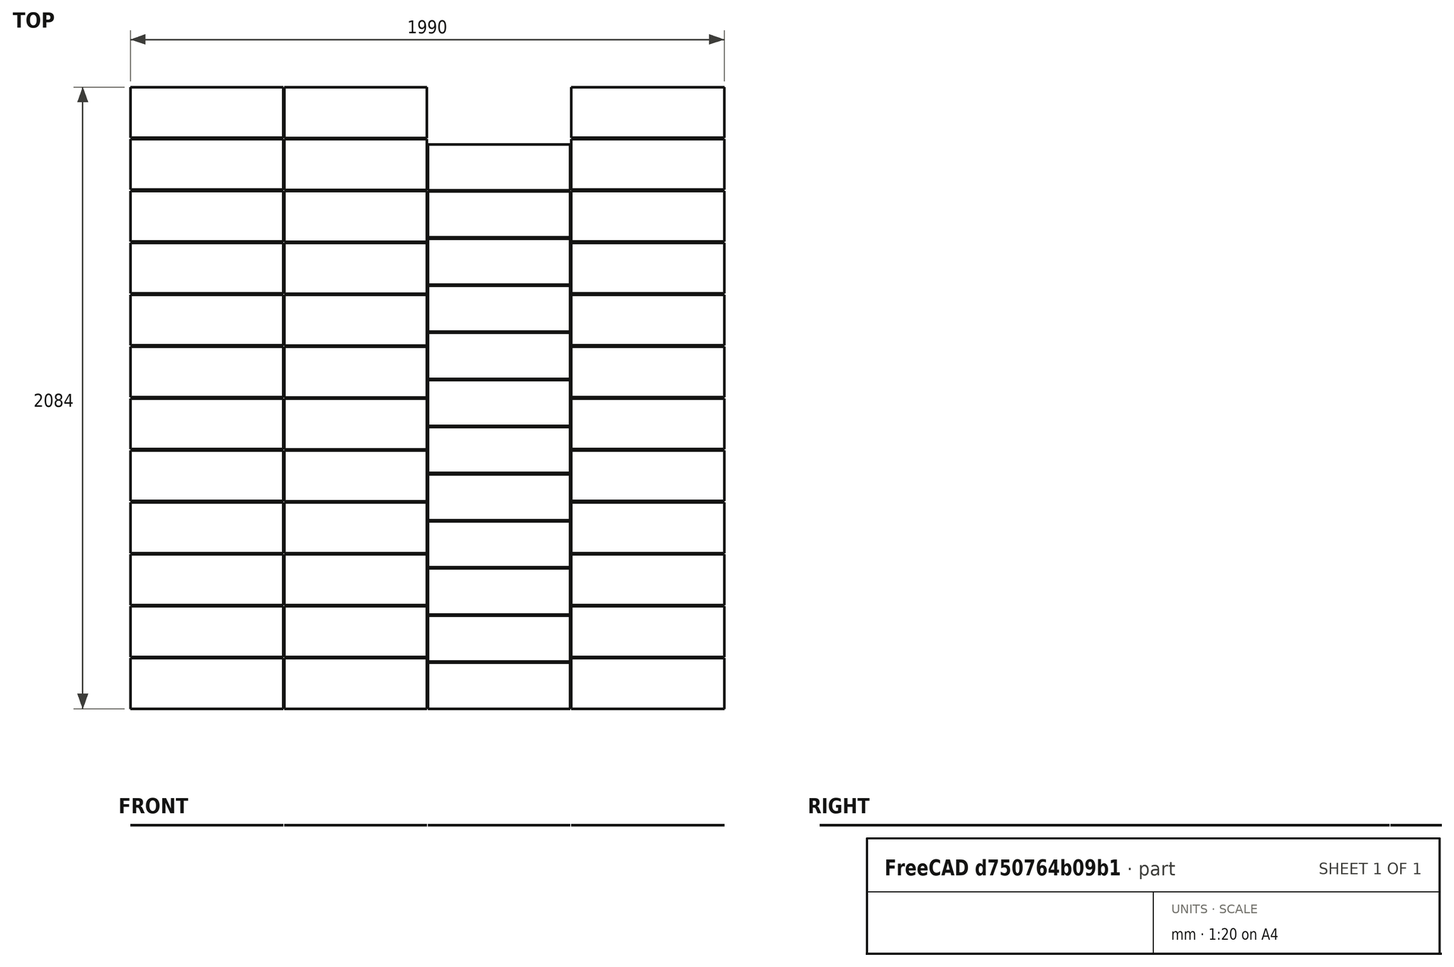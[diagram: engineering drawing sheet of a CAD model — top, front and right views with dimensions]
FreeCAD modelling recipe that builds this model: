
FCSTD DOCUMENT  (FreeCAD 1.0RUnknown)
Label: Schnittplan
License: All rights reserved
LicenseURL: https://en.wikipedia.org/wiki/All_rights_reserved
objects: Part::Part2DObjectPython×34, App::FeaturePython×28, Part::FeaturePython×4
note: 38 computed .brp shape members not serialized (recipe doc carries the construction recipe); baked Part::Feature solids carry a one-line shape summary decoded from their .brp

FEATURE [Part::Part2DObjectPython] Rectangle  label="3-Schichtplatte Fichte 19mm"  # Draft 2D object (typed FeaturePython)
  Area = 10250000
  ChamferSize = 0
  Columns = 1
  FilletRadius = 0
  Height = 5000
  Length = 2050
  MakeFace = true
  Rows = 1
FEATURE [Part::Part2DObjectPython] Rectangle001  label="Seitenteil Korpus 1"  # Draft 2D object (typed FeaturePython)
  Area = 1204200
  ChamferSize = 0
  Columns = 1
  FilletRadius = 0
  Height = 2007
  Length = 600
  MakeFace = true
  Placement = pos=(0,600,0) rot=(0,0,1;-1.5708rad)
  Rows = 1
FEATURE [Part::Part2DObjectPython] Rectangle002  label="Seitenteil Korpus 1.1"  # Draft 2D object (typed FeaturePython)
  Area = 1204200
  ChamferSize = 0
  Columns = 1
  FilletRadius = 0
  Height = 2007
  Length = 600
  MakeFace = true
  Placement = pos=(0,1204,0) rot=(0,0,1;-1.5708rad)
  Rows = 1
FEATURE [Part::Part2DObjectPython] Rectangle003  label="Tür Korpus 2"  # Draft 2D object (typed FeaturePython)
  Area = 1094610
  ChamferSize = 0
  Columns = 1
  FilletRadius = 0
  Height = 2046
  Length = 535
  MakeFace = true
  Placement = pos=(0,1743,0) rot=(0,0,1;-1.5708rad)
  Rows = 1
FEATURE [Part::Part2DObjectPython] Rectangle004  label="Tür Korpus 1"  # Draft 2D object (typed FeaturePython)
  Area = 1305400
  ChamferSize = 0
  Columns = 1
  FilletRadius = 0
  Height = 2440
  Length = 535
  MakeFace = true
  Placement = pos=(0,1747,0) rot=(0,0,1;0rad)
  Rows = 1
FEATURE [Part::Part2DObjectPython] Rectangle005  label="Rückplatte Korpus 1"  # Draft 2D object (typed FeaturePython)
  Area = 1104300
  ChamferSize = 0
  Columns = 1
  FilletRadius = 0
  Height = 2045
  Length = 540
  MakeFace = true
  Placement = pos=(2100,540,0) rot=(0,0,1;-1.5708rad)
  Rows = 1
FEATURE [Part::Part2DObjectPython] Rectangle006  label="Rückplatte Korpus 2"  # Draft 2D object (typed FeaturePython)
  Area = 764100
  ChamferSize = 0
  Columns = 1
  FilletRadius = 0
  Height = 1415
  Length = 540
  MakeFace = true
  Placement = pos=(539,4034,0) rot=(0,0,1;-1.5708rad)
  Rows = 1
FEATURE [Part::Part2DObjectPython] Rectangle007  label="Rückplatte Korpus 3"  # Draft 2D object (typed FeaturePython)
  Area = 421200
  ChamferSize = 0
  Columns = 1
  FilletRadius = 0
  Height = 780
  Length = 540
  MakeFace = true
  Placement = pos=(3188,3776,0) rot=(0,0,1;-1.5708rad)
  Rows = 1
FEATURE [Part::Part2DObjectPython] Rectangle008  label="Tür Korpus 3"  # Draft 2D object (typed FeaturePython)
  Area = 756490
  ChamferSize = 0
  Columns = 1
  FilletRadius = 0
  Height = 1414
  Length = 535
  MakeFace = true
  Placement = pos=(539,2282,0) rot=(0,0,1;-1.5708rad)
  Rows = 1
FEATURE [Part::Part2DObjectPython] Rectangle009  label="Tür Korpus 4"  # Draft 2D object (typed FeaturePython)
  Area = 402730
  ChamferSize = 0
  Columns = 1
  FilletRadius = 0
  Height = 782
  Length = 515
  MakeFace = true
  Placement = pos=(0,4191,0) rot=(0,0,1;0rad)
  Rows = 1
FEATURE [Part::Part2DObjectPython] Rectangle010  label="Rückplatte Korpus 4"  # Draft 2D object (typed FeaturePython)
  Area = 408200
  ChamferSize = 0
  Columns = 1
  FilletRadius = 0
  Height = 785
  Length = 520
  MakeFace = true
  Placement = pos=(2704,4964,0) rot=(0,0,1;-1.5708rad)
  Rows = 1
FEATURE [Part::Part2DObjectPython] Rectangle011  label="Seitenteil Korpus 2"  # Draft 2D object (typed FeaturePython)
  Area = 826200
  ChamferSize = 0
  Columns = 1
  FilletRadius = 0
  Height = 1377
  Length = 600
  MakeFace = true
  Placement = pos=(539,2886,0) rot=(0,0,1;-1.5708rad)
  Rows = 1
FEATURE [Part::Part2DObjectPython] Rectangle012  label="Seitenteil Korpus 2.1"  # Draft 2D object (typed FeaturePython)
  Area = 826200
  ChamferSize = 0
  Columns = 1
  FilletRadius = 0
  Height = 1377
  Length = 600
  MakeFace = true
  Placement = pos=(539,3490,0) rot=(0,0,1;-1.5708rad)
  Rows = 1
FEATURE [Part::Part2DObjectPython] Rectangle013  label="3-Schichtplatte Fichte 19mm001"  # Draft 2D object (typed FeaturePython)
  Area = 10250000
  ChamferSize = 0
  Columns = 1
  FilletRadius = 0
  Height = 5000
  Length = 2050
  MakeFace = true
  Placement = pos=(2100,0,0) rot=(0,0,1;0rad)
  Rows = 1
FEATURE [Part::Part2DObjectPython] Rectangle014  label="Seitenteil Korpus 3"  # Draft 2D object (typed FeaturePython)
  Area = 445200
  ChamferSize = 0
  Columns = 1
  FilletRadius = 0
  Height = 742
  Length = 600
  MakeFace = true
  Placement = pos=(2100,3232,0) rot=(0,0,1;-1.5708rad)
  Rows = 1
FEATURE [Part::Part2DObjectPython] Rectangle015  label="Seitenteil Korpus 3.1"  # Draft 2D object (typed FeaturePython)
  Area = 445200
  ChamferSize = 0
  Columns = 1
  FilletRadius = 0
  Height = 742
  Length = 600
  MakeFace = true
  Placement = pos=(2846,3232,0) rot=(0,0,1;-1.5708rad)
  Rows = 1
FEATURE [Part::Part2DObjectPython] Rectangle016  label="Schublade Seitenteile"  # Draft 2D object (typed FeaturePython)
  Area = 87040
  ChamferSize = 0
  Columns = 1
  FilletRadius = 0
  Height = 170
  Length = 512
  MakeFace = true
  Placement = pos=(3592,544,0) rot=(0,0,1;0rad)
  Rows = 1
FEATURE [Part::Part2DObjectPython] Line  # Draft 2D object (typed FeaturePython)
  Area = 0
  ChamferSize = 0
  Closed = false
  End = (2100,2458,0)
  FilletRadius = 0
  Length = 1914
  MakeFace = true
  Placement = pos=(2345.23,716.413,0) rot=(0,0,1;0rad)
  Points = (2) [(-245.23,-172.413,0),(-245.23,1741.59,0)]
  Start = (2100,544,0)
  Subdivisions = 0
FEATURE [Part::FeaturePython] PathArray  # WARN: FeaturePython — macro-defined, semantics opaque (R4)
  Align = false
  AlignMode = 0
  Base = -> Rectangle016
  Count = 12
  EndOffset = 0
  ExtraTranslation = (0,0,0)
  ForceVertical = false
  Fuse = false
  PathObject = -> Line
  StartOffset = 0
  TangentVector = (1,0,0)
  VerticalVector = (0,0,1)
FEATURE [Part::Part2DObjectPython] Rectangle017  label="Schublade Fronten"  # Draft 2D object (typed FeaturePython)
  Area = 81090
  ChamferSize = 0
  Columns = 1
  FilletRadius = 0
  Height = 170
  Length = 477
  MakeFace = true
  Placement = pos=(3111,1148,0) rot=(0,0,1;0rad)
  Rows = 1
FEATURE [Part::Part2DObjectPython] Line001  # Draft 2D object (typed FeaturePython)
  Area = 0
  ChamferSize = 0
  Closed = false
  End = (2616,2457.4,0)
  FilletRadius = 0
  Length = 1913.4
  MakeFace = true
  Placement = pos=(2616,564,0) rot=(0,0,1;0rad)
  Points = (2) [(0,-20,0),(0,1893.4,0)]
  Start = (2616,544,0)
  Subdivisions = 0
FEATURE [Part::FeaturePython] PathArray001  # WARN: FeaturePython — macro-defined, semantics opaque (R4)
  Align = false
  AlignMode = 0
  Base = -> Rectangle017
  Count = 12
  EndOffset = 0
  ExtraTranslation = (0,0,0)
  ForceVertical = false
  Fuse = false
  PathObject = -> Line001
  StartOffset = 0
  TangentVector = (1,0,0)
  VerticalVector = (0,0,1)
FEATURE [Part::Part2DObjectPython] Rectangle018  label="Schublade Rückplatten"  # Draft 2D object (typed FeaturePython)
  Area = 73458
  ChamferSize = 0
  Columns = 1
  FilletRadius = 0
  Height = 154
  Length = 477
  MakeFace = true
  Placement = pos=(2630,1148,0) rot=(0,0,1;0rad)
  Rows = 1
FEATURE [Part::Part2DObjectPython] Line002  # Draft 2D object (typed FeaturePython)
  Area = 0
  ChamferSize = 0
  Closed = false
  End = (3097,2282,0)
  FilletRadius = 0
  Length = 1738
  MakeFace = true
  Placement = pos=(3100,589,0) rot=(0,0,1;0rad)
  Points = (2) [(-3,-45,0),(-3,1693,0)]
  Start = (3097,544,0)
  Subdivisions = 0
FEATURE [Part::FeaturePython] PathArray002  # WARN: FeaturePython — macro-defined, semantics opaque (R4)
  Align = false
  AlignMode = 0
  Base = -> Rectangle018
  Count = 12
  EndOffset = 0
  ExtraTranslation = (0,0,0)
  ForceVertical = false
  Fuse = false
  PathObject = -> Line002
  StartOffset = 0
  TangentVector = (1,0,0)
  VerticalVector = (0,0,1)
FEATURE [Part::Part2DObjectPython] Line003  # Draft 2D object (typed FeaturePython)
  Area = 0
  ChamferSize = 0
  Closed = false
  End = (3578,2458,0)
  FilletRadius = 0
  Length = 1914
  MakeFace = true
  Placement = pos=(3826,716,0) rot=(0,0,1;0rad)
  Points = (2) [(-248,-172,0),(-248,1742,0)]
  Start = (3578,544,0)
  Subdivisions = 0
FEATURE [Part::Part2DObjectPython] Rectangle019  label="Schublade Seitenteile001"  # Draft 2D object (typed FeaturePython)
  Area = 87040
  ChamferSize = 0
  Columns = 1
  FilletRadius = 0
  Height = 170
  Length = 512
  MakeFace = true
  Placement = pos=(3592,544,0) rot=(0,0,1;0rad)
  Rows = 1
FEATURE [Part::FeaturePython] PathArray003  # WARN: FeaturePython — macro-defined, semantics opaque (R4)
  Align = false
  AlignMode = 0
  Base = -> Rectangle019
  Count = 12
  EndOffset = 0
  ExtraTranslation = (0,0,0)
  ForceVertical = false
  Fuse = false
  PathObject = -> Line003
  StartOffset = 0
  TangentVector = (1,0,0)
  VerticalVector = (0,0,1)
FEATURE [Part::Part2DObjectPython] Rectangle020  label="Deckplatten Korpus 1-3"  # Draft 2D object (typed FeaturePython)
  Area = 324000
  ChamferSize = 0
  Columns = 1
  FilletRadius = 0
  Height = 540
  Length = 600
  MakeFace = true
  Placement = pos=(3592,3232,0) rot=(0,0,1;-1.5708rad)
  Rows = 1
FEATURE [Part::Part2DObjectPython] Rectangle021  label="Deckplatten Korpus 1-3.1"  # Draft 2D object (typed FeaturePython)
  Area = 324000
  ChamferSize = 0
  Columns = 1
  FilletRadius = 0
  Height = 540
  Length = 600
  MakeFace = true
  Placement = pos=(2100,4440,0) rot=(0,0,1;-1.5708rad)
  Rows = 1
FEATURE [Part::Part2DObjectPython] Rectangle022  label="Deckplatten Korpus 1-3.2"  # Draft 2D object (typed FeaturePython)
  Area = 324000
  ChamferSize = 0
  Columns = 1
  FilletRadius = 0
  Height = 540
  Length = 600
  MakeFace = true
  Placement = pos=(2644,4440,0) rot=(0,0,1;-1.5708rad)
  Rows = 1
FEATURE [Part::Part2DObjectPython] Rectangle023  label="Grundplatten Korpus 1-3"  # Draft 2D object (typed FeaturePython)
  Area = 324000
  ChamferSize = 0
  Columns = 1
  FilletRadius = 0
  Height = 540
  Length = 600
  MakeFace = true
  Placement = pos=(2644,3836,0) rot=(0,0,1;-1.5708rad)
  Rows = 1
FEATURE [Part::Part2DObjectPython] Rectangle024  label="Grundplatten Korpus 1-3.1"  # Draft 2D object (typed FeaturePython)
  Area = 324000
  ChamferSize = 0
  Columns = 1
  FilletRadius = 0
  Height = 540
  Length = 600
  MakeFace = true
  Placement = pos=(3188,4380,0) rot=(0,0,1;-1.5708rad)
  Rows = 1
FEATURE [Part::Part2DObjectPython] Rectangle025  label="Grundplatten Korpus 1-3.2"  # Draft 2D object (typed FeaturePython)
  Area = 324000
  ChamferSize = 0
  Columns = 1
  FilletRadius = 0
  Height = 540
  Length = 600
  MakeFace = true
  Placement = pos=(2100,3836,0) rot=(0,0,1;-1.5708rad)
  Rows = 1
FEATURE [Part::Part2DObjectPython] Rectangle026  label="Deckplatte Korpus 4"  # Draft 2D object (typed FeaturePython)
  Area = 493800
  ChamferSize = 0
  Columns = 1
  FilletRadius = 0
  Height = 823
  Length = 600
  MakeFace = true
  Placement = pos=(539,4038,0) rot=(0,0,1;0rad)
  Rows = 1
FEATURE [Part::Part2DObjectPython] Rectangle027  label="Grundplatte Korpus 4"  # Draft 2D object (typed FeaturePython)
  Area = 312000
  ChamferSize = 0
  Columns = 1
  FilletRadius = 0
  Height = 520
  Length = 600
  MakeFace = true
  Placement = pos=(2100,4444,0) rot=(0,0,1;0rad)
  Rows = 1
FEATURE [Part::Part2DObjectPython] Rectangle028  label="Linkes Seitenteil Korpus 4"  # Draft 2D object (typed FeaturePython)
  Area = 90000
  ChamferSize = 0
  Columns = 1
  FilletRadius = 0
  Height = 150
  Length = 600
  MakeFace = true
  Placement = pos=(3882,3780,0) rot=(0,0,1;1.5708rad)
  Rows = 1
FEATURE [Part::Part2DObjectPython] Rectangle029  label="Rechtes Seitenteil Korpus 4"  # Draft 2D object (typed FeaturePython)
  Area = 442200
  ChamferSize = 0
  Columns = 1
  FilletRadius = 0
  Height = 737
  Length = 600
  MakeFace = true
  Placement = pos=(1143,4038,0) rot=(0,0,1;0rad)
  Rows = 1
FEATURE [App::FeaturePython] Text  # WARN: FeaturePython — macro-defined, semantics opaque (R4)
  Placement = pos=(800,250,0) rot=(0,0,1;0rad)
  Text = 2007x600
FEATURE [App::FeaturePython] Text001  # WARN: FeaturePython — macro-defined, semantics opaque (R4)
  Placement = pos=(800,850,0) rot=(0,0,1;0rad)
  Text = 2007x600
FEATURE [App::FeaturePython] Text002  # WARN: FeaturePython — macro-defined, semantics opaque (R4)
  Placement = pos=(800,1450,0) rot=(0,0,1;0rad)
  Text = 2046x535
FEATURE [App::FeaturePython] Text003  # WARN: FeaturePython — macro-defined, semantics opaque (R4)
  Placement = pos=(1008,1950,0) rot=(0,0,1;0rad)
  Text = 1414x535
FEATURE [App::FeaturePython] Text004  # WARN: FeaturePython — macro-defined, semantics opaque (R4)
  Placement = pos=(978,2550,0) rot=(0,0,1;0rad)
  Text = 1377x600
FEATURE [App::FeaturePython] Text005  # WARN: FeaturePython — macro-defined, semantics opaque (R4)
  Placement = pos=(978,3150,0) rot=(0,0,1;0rad)
  Text = 1377x600
FEATURE [App::FeaturePython] Text006  # WARN: FeaturePython — macro-defined, semantics opaque (R4)
  Placement = pos=(978,3700,0) rot=(0,0,1;0rad)
  Text = 1415x540
FEATURE [App::FeaturePython] Text007  # WARN: FeaturePython — macro-defined, semantics opaque (R4)
  Placement = pos=(300,2900,0) rot=(0,0,1;1.5708rad)
  Text = 2440x535
FEATURE [App::FeaturePython] Text008  # WARN: FeaturePython — macro-defined, semantics opaque (R4)
  Placement = pos=(1213,4350,0) rot=(0,0,1;0rad)
  Text = 737x600
FEATURE [App::FeaturePython] Text009  # WARN: FeaturePython — macro-defined, semantics opaque (R4)
  Placement = pos=(620,4350,0) rot=(0,0,1;0rad)
  Text = 823x600
FEATURE [App::FeaturePython] Text010  # WARN: FeaturePython — macro-defined, semantics opaque (R4)
  Placement = pos=(70,4507,0) rot=(0,0,1;0rad)
  Text = 782x515
FEATURE [App::FeaturePython] Text011  # WARN: FeaturePython — macro-defined, semantics opaque (R4)
  Placement = pos=(2800,250,0) rot=(0,0,1;0rad)
  Text = 2045x540
FEATURE [App::FeaturePython] Text012  # WARN: FeaturePython — macro-defined, semantics opaque (R4)
  Placement = pos=(2400,1200,0) rot=(0,0,1;1.5708rad)
  Text = 12x  512x170
FEATURE [App::FeaturePython] Text013  # WARN: FeaturePython — macro-defined, semantics opaque (R4)
  Placement = pos=(3850,1200,0) rot=(0,0,1;1.5708rad)
  Text = 12x  512x170
FEATURE [App::FeaturePython] Text014  # WARN: FeaturePython — macro-defined, semantics opaque (R4)
  Placement = pos=(3350,1172,0) rot=(0,0,1;1.5708rad)
  Text = 12x  477x154
FEATURE [App::FeaturePython] Text015  # WARN: FeaturePython — macro-defined, semantics opaque (R4)
  Placement = pos=(2898,1168,0) rot=(0,0,1;1.5708rad)
  Text = 12x  477x170
FEATURE [App::FeaturePython] Text016  # WARN: FeaturePython — macro-defined, semantics opaque (R4)
  Placement = pos=(2259,2900,0) rot=(0,0,1;0rad)
  Text = 742x600
FEATURE [App::FeaturePython] Text017  # WARN: FeaturePython — macro-defined, semantics opaque (R4)
  Placement = pos=(3000,2900,0) rot=(0,0,1;0rad)
  Text = 742x600
FEATURE [App::FeaturePython] Text018  # WARN: FeaturePython — macro-defined, semantics opaque (R4)
  Placement = pos=(3650,2900,0) rot=(0,0,1;0rad)
  Text = 540x600
FEATURE [App::FeaturePython] Text019  # WARN: FeaturePython — macro-defined, semantics opaque (R4)
  Placement = pos=(3350,3450,0) rot=(0,0,1;0rad)
  Text = 780x540
FEATURE [App::FeaturePython] Text020  # WARN: FeaturePython — macro-defined, semantics opaque (R4)
  Placement = pos=(2700,3502,0) rot=(0,0,1;0rad)
  Text = 600x540
FEATURE [App::FeaturePython] Text021  # WARN: FeaturePython — macro-defined, semantics opaque (R4)
  Placement = pos=(2150,3506,0) rot=(0,0,1;0rad)
  Text = 600x540
FEATURE [App::FeaturePython] Text022  # WARN: FeaturePython — macro-defined, semantics opaque (R4)
  Placement = pos=(2150,4106,0) rot=(0,0,1;0rad)
  Text = 600x540
FEATURE [App::FeaturePython] Text023  # WARN: FeaturePython — macro-defined, semantics opaque (R4)
  Placement = pos=(2700,4106,0) rot=(0,0,1;0rad)
  Text = 600x540
FEATURE [App::FeaturePython] Text024  # WARN: FeaturePython — macro-defined, semantics opaque (R4)
  Placement = pos=(3250,4044,0) rot=(0,0,1;0rad)
  Text = 600x540
FEATURE [App::FeaturePython] Text025  # WARN: FeaturePython — macro-defined, semantics opaque (R4)
  Placement = pos=(2174,4650,0) rot=(0,0,1;0rad)
  Text = 600x520
FEATURE [App::FeaturePython] Text026  # WARN: FeaturePython — macro-defined, semantics opaque (R4)
  Placement = pos=(2893,4650,0) rot=(0,0,1;0rad)
  Text = 785x520
FEATURE [App::FeaturePython] Text027  # WARN: FeaturePython — macro-defined, semantics opaque (R4)
  Placement = pos=(3847,3878,0) rot=(0,0,1;1.5708rad)
  Text = 600x150
